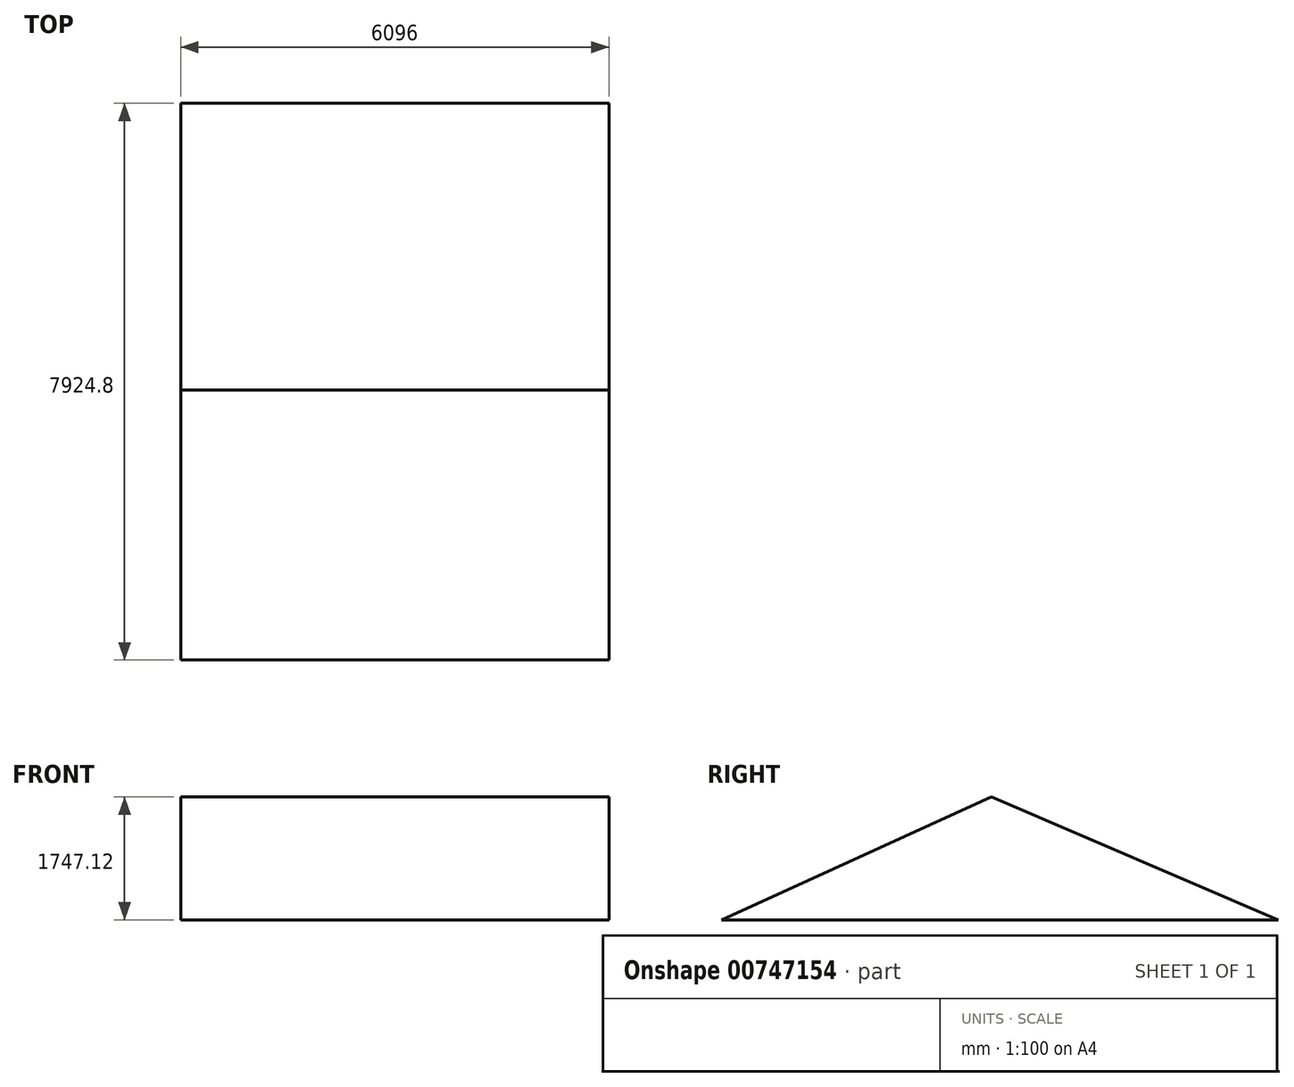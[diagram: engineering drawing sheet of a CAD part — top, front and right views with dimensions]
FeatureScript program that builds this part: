
annotation { "Feature Type Name" : "Feature", "Feature Type Description" : "" }
export const myFeature = defineFeature(function(context is Context, id is Id, definition is map)
    precondition{}
    {
        {
            var Q0;
            Q0=qCreatedBy(makeId("Right.planeOp"),FACE);
            var sketch = newSketch(context, id + "F0", { "sketchPlane" : qUnion([Q0])});
            skLineSegment(sketch, "E0", {"start": v(-3846.57, 680.5) * mm, "end": v(4078.23, 680.5) * mm});
            skLineSegment(sketch, "E1", {"start": v(-3846.57, 680.5) * mm, "end": v(0, 2427.63) * mm});
            skLineSegment(sketch, "E2", {"start": v(0, 2427.63) * mm, "end": v(4078.23, 680.5) * mm});
            skSolve(sketch);
        }
        {
            var Q0;
            Q0 = qSketchRegion(id + "F0", true);
            extrude(context, id + "F1", {"entities" : qUnion([Q0]), "oppositeDirection" : true, "depth" : 6096 * mm, "offsetDistance" : 25.4 * mm});
        }
    });
